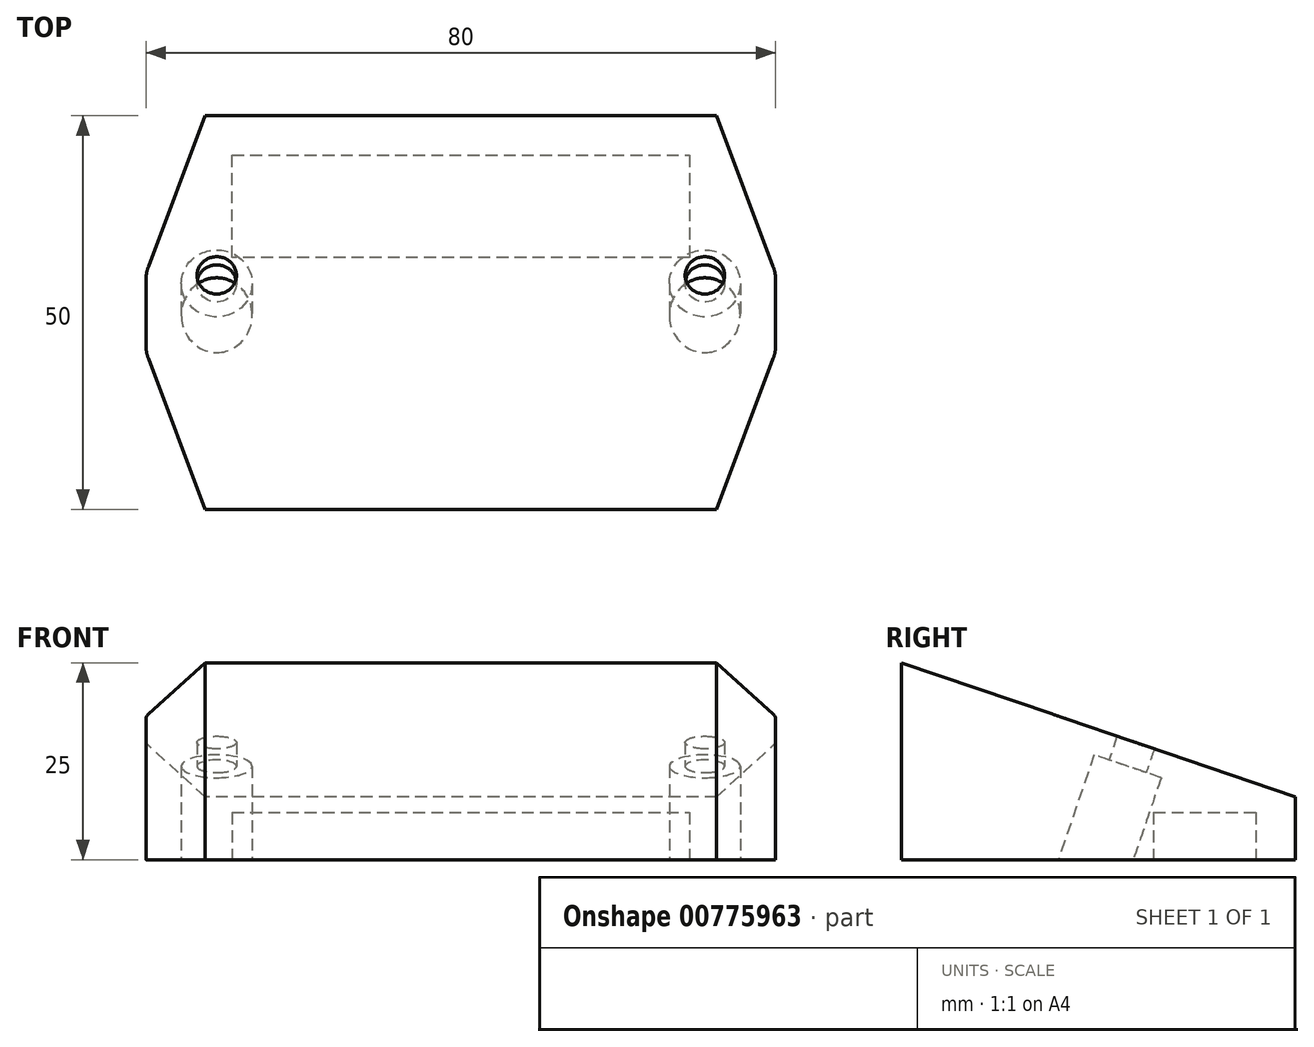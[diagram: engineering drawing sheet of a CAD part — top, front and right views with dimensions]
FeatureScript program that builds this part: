
annotation { "Feature Type Name" : "Feature", "Feature Type Description" : "" }
export const myFeature = defineFeature(function(context is Context, id is Id, definition is map)
    precondition{}
    {
        {
            var Q0;
            Q0=qCreatedBy(makeId("Right.planeOp"),FACE);
            var sketch = newSketch(context, id + "F0", { "sketchPlane" : qUnion([Q0])});
            skLineSegment(sketch, "E0", {"start": v(0, 0) * mm, "end": v(50, 0) * mm});
            skLineSegment(sketch, "E1", {"start": v(0, 0) * mm, "end": v(0, 25) * mm});
            skLineSegment(sketch, "E2", {"start": v(50, 0) * mm, "end": v(50, 8) * mm});
            skLineSegment(sketch, "E3", {"start": v(0, 25) * mm, "end": v(50, 8) * mm});
            skSolve(sketch);
        }
        {
            var Q0;
            Q0=makeQuery(id+"F0.imprint","IMPRINT",FACE,{"disambiguationData":[TD([[makeQuery(id+"F0.imprint","IMPRINT",EDGE,{"derivedFrom":sQuery(id+"F0.wireOp",EDGE,"E0")}),1.0]])]});
            extrude(context, id + "F1", {"entities" : qUnion([Q0]), "depth" : 80 * mm, "offsetDistance" : 25 * mm});
        }
        {
            var Q0;
            Q0=makeQuery(id+"F1.opExtrude","SWEPT_FACE",FACE,{"disambiguationData":[OSD([sQuery(id+"F0.wireOp",EDGE,"E0")])]});
            var sketch = newSketch(context, id + "F2", { "sketchPlane" : qUnion([Q0])});
            skLineSegment(sketch, "E4", {"start": v(0, -25) * mm, "end": v(80, -25) * mm, "construction": true});
            skLineSegment(sketch, "E5.0", {"start": v(0, -30) * mm, "end": v(80, -30) * mm, "construction": true});
            skLineSegment(sketch, "E6.0", {"start": v(0, -20) * mm, "end": v(80, -20) * mm, "construction": true});
            skLineSegment(sketch, "E7.0", {"start": v(71, 4) * mm, "end": v(71, -54) * mm, "construction": true});
            skLineSegment(sketch, "E8.0", {"start": v(9, 4) * mm, "end": v(9, -54) * mm, "construction": true});
            skLineSegment(sketch, "E9", {"start": v(7.78, 0.76) * mm, "end": v(0.32, -19.15) * mm});
            skLineSegment(sketch, "E10", {"start": v(0.32, -30.85) * mm, "end": v(7.78, -50.76) * mm});
            skLineSegment(sketch, "E11", {"start": v(72.22, 0.76) * mm, "end": v(79.68, -19.15) * mm});
            skLineSegment(sketch, "E12", {"start": v(79.68, -30.85) * mm, "end": v(72.22, -50.76) * mm});
            skLineSegment(sketch, "E13", {"start": v(12.47, 4) * mm, "end": v(67.53, 4) * mm});
            skLineSegment(sketch, "E14", {"start": v(80, -20.9) * mm, "end": v(80, -29.1) * mm});
            skLineSegment(sketch, "E15", {"start": v(67.53, -54) * mm, "end": v(12.47, -54) * mm});
            skLineSegment(sketch, "E16", {"start": v(0, -29.1) * mm, "end": v(0, -20.9) * mm});
            skPoint(sketch, "E17.visualSharp", {"position": v(9, 4) * mm});
            skArc(sketch, "E17.filletArc", {"start": v(12.47, 4) * mm, "mid": v(9.62, 3.1) * mm, "end": v(7.78, 0.76) * mm});
            skPoint(sketch, "E18.visualSharp", {"position": v(71, 4) * mm});
            skArc(sketch, "E18.filletArc", {"start": v(72.22, 0.76) * mm, "mid": v(70.38, 3.1) * mm, "end": v(67.53, 4) * mm});
            skPoint(sketch, "E19.visualSharp", {"position": v(71, -54) * mm});
            skArc(sketch, "E19.filletArc", {"start": v(67.53, -54) * mm, "mid": v(70.38, -53.1) * mm, "end": v(72.22, -50.76) * mm});
            skPoint(sketch, "E20.visualSharp", {"position": v(9, -54) * mm});
            skArc(sketch, "E20.filletArc", {"start": v(7.78, -50.76) * mm, "mid": v(9.62, -53.1) * mm, "end": v(12.47, -54) * mm});
            skPoint(sketch, "E21.visualSharp", {"position": v(80, -30) * mm});
            skArc(sketch, "E21.filletArc", {"start": v(79.68, -30.85) * mm, "mid": v(79.92, -29.99) * mm, "end": v(80, -29.1) * mm});
            skPoint(sketch, "E22.visualSharp", {"position": v(80, -20) * mm});
            skArc(sketch, "E22.filletArc", {"start": v(80, -20.9) * mm, "mid": v(79.92, -20.01) * mm, "end": v(79.68, -19.15) * mm});
            skPoint(sketch, "E23.visualSharp", {"position": v(0, -20) * mm});
            skArc(sketch, "E23.filletArc", {"start": v(0.32, -19.15) * mm, "mid": v(0.08, -20.01) * mm, "end": v(0, -20.9) * mm});
            skPoint(sketch, "E24.visualSharp", {"position": v(0, -30) * mm});
            skArc(sketch, "E24.filletArc", {"start": v(0, -29.1) * mm, "mid": v(0.08, -29.99) * mm, "end": v(0.32, -30.85) * mm});
            skSolve(sketch);
        }
        {
            var Q0;
            {var subQ0=sQuery(id+"F2.wireOp",EDGE,"E9");Q0=makeQuery(id+"F2.imprint","IMPRINT",FACE,{"disambiguationData":[TD([[makeQuery(id+"F2.imprint","IMPRINT",EDGE,{"derivedFrom":subQ0}),-1.0]])]});}
            var Q1;
            {var subQ0=sQuery(id+"F2.wireOp",EDGE,"E10");Q1=makeQuery(id+"F2.imprint","IMPRINT",FACE,{"disambiguationData":[TD([[makeQuery(id+"F2.imprint","IMPRINT",EDGE,{"derivedFrom":subQ0}),-1.0]])]});}
            var Q2;
            {var subQ0=sQuery(id+"F2.wireOp",EDGE,"E12");Q2=makeQuery(id+"F2.imprint","IMPRINT",FACE,{"disambiguationData":[TD([[makeQuery(id+"F2.imprint","IMPRINT",EDGE,{"derivedFrom":subQ0}),1.0]])]});}
            var Q3;
            {var subQ0=sQuery(id+"F2.wireOp",EDGE,"E11");Q3=makeQuery(id+"F2.imprint","IMPRINT",FACE,{"disambiguationData":[TD([[makeQuery(id+"F2.imprint","IMPRINT",EDGE,{"derivedFrom":subQ0}),1.0]])]});}
            extrude(context, id + "F3", {"entities" : qUnion([Q0, Q1, Q2, Q3]), "operationType" : NewBodyOperationType.REMOVE, "oppositeDirection" : true, "depth" : 25 * mm, "offsetDistance" : 25 * mm});
        }
        {
            var Q0;
            Q0=makeQuery(id+"F1.opExtrude","SWEPT_FACE",FACE,{"disambiguationData":[OSD([sQuery(id+"F0.wireOp",EDGE,"E3")])]});
            var Q1;
            Q1 = qBodyType(qCreatedBy(id + "F5" ,EDGE), BodyType.WIRE);
            cPlane(context, id + "F4", {"entities" : qUnion([Q0, Q1]), "cplaneType" : CPlaneType.OFFSET, "offset" : 18 * mm, "oppositeDirection" : true, "width" : 150 * mm, "height" : 150 * mm});
        }
        {
            var Q0;
            Q0=qCreatedBy(id+"F4.planeOp",FACE);
            var sketch = newSketch(context, id + "F5", { "sketchPlane" : qUnion([Q0])});
            skLineSegment(sketch, "E25.0", {"start": v(9, 14.03) * mm, "end": v(9, 22.68) * mm});
            skLineSegment(sketch, "E26.0", {"start": v(71, 14.03) * mm, "end": v(71, 22.68) * mm});
            skLineSegment(sketch, "E27", {"start": v(9, 18.36) * mm, "end": v(71, 18.36) * mm});
            skLineSegment(sketch, "E28.0", {"start": v(9, 23.36) * mm, "end": v(71, 23.36) * mm});
            skSolve(sketch);
        }
        {
            var Q0;
            Q0=sQuery(id+"F5.wireOp",VERTEX,"E28.0.end");
            var Q1;
            Q1=sQuery(id+"F5.wireOp",VERTEX,"E28.0.start");
            var Q2;
            Q2=makeQuery(id+"F1.opExtrude","SWEPT_BODY",BODY,{"disambiguationData":[OSD([sQuery(id+"F0.wireOp",EDGE,"E0"),sQuery(id+"F0.wireOp",EDGE,"E1"),sQuery(id+"F0.wireOp",EDGE,"E2"),sQuery(id+"F0.wireOp",EDGE,"E3")])]});
            hole(context, id + "F6", {"style" : HoleStyle.C_BORE, "endStyle" : HoleEndStyle.THROUGH, "oppositeDirection" : true, "holeDiameter" : 5 * mm, "cBoreDiameter" : 9 * mm, "cBoreDepth" : 11 * mm, "majorDiameter" : 5 * mm, "isTappedThrough" : true, "tappedDepth" : 12 * mm, "tapClearance" : 3, "locations" : qUnion([Q0, Q1]), "scope" : qUnion([Q2])});
        }
        {
            var Q0;
            Q0=makeQuery(id+"F1.opExtrude","SWEPT_FACE",FACE,{"disambiguationData":[OSD([sQuery(id+"F0.wireOp",EDGE,"E0")])]});
            var sketch = newSketch(context, id + "F7", { "sketchPlane" : qUnion([Q0])});
            skLineSegment(sketch, "E29.left", {"start": v(0.32, -30.85) * mm, "end": v(0.32, -30.85) * mm});
            skLineSegment(sketch, "E29.right", {"start": v(79.68, -30.85) * mm, "end": v(79.68, -30.85) * mm});
            skPoint(sketch, "E30.oppositeSnap0", {"position": v(71, -29.42) * mm});
            skLineSegment(sketch, "E31", {"start": v(10.97, -45) * mm, "end": v(69.03, -45) * mm});
            skLineSegment(sketch, "E32", {"start": v(69.03, -45) * mm, "end": v(69.03, -32) * mm});
            skLineSegment(sketch, "E33", {"start": v(69.03, -32) * mm, "end": v(10.97, -32) * mm});
            skLineSegment(sketch, "E34", {"start": v(10.97, -32) * mm, "end": v(10.97, -45) * mm});
            skSolve(sketch);
        }
        {
            var Q0;
            Q0=makeQuery(id+"F7.imprint","IMPRINT",FACE,{"disambiguationData":[TD([[makeQuery(id+"F7.imprint","IMPRINT",EDGE,{"derivedFrom":sQuery(id+"F7.wireOp",EDGE,"E31")}),1.0]])]});
            extrude(context, id + "F8", {"entities" : qUnion([Q0]), "operationType" : NewBodyOperationType.REMOVE, "oppositeDirection" : true, "depth" : 6 * mm, "offsetDistance" : 25 * mm});
        }
    });
